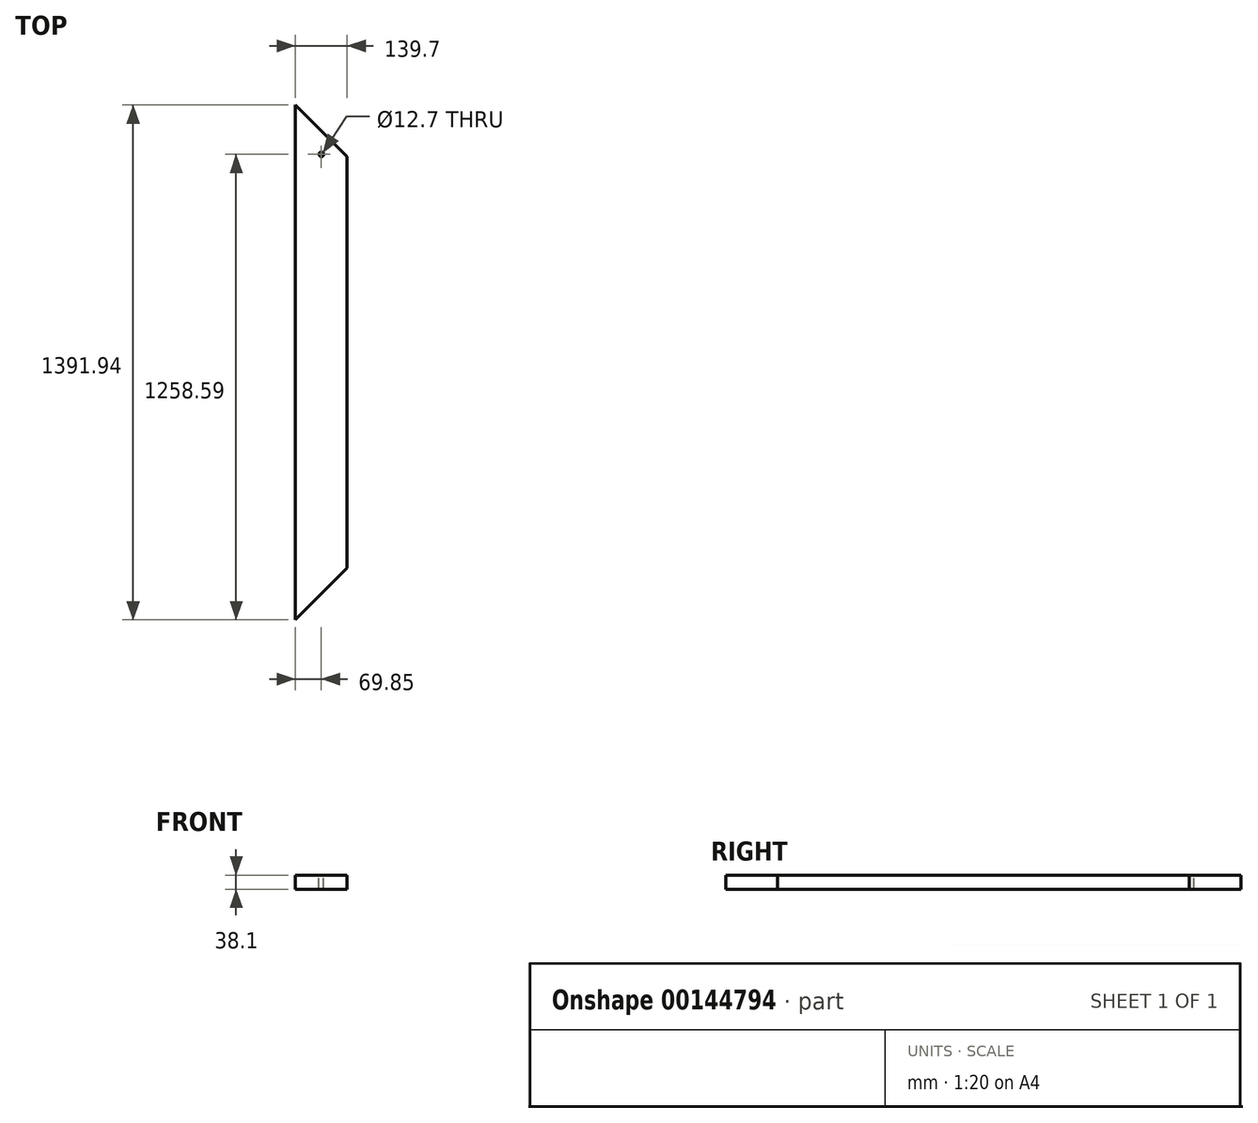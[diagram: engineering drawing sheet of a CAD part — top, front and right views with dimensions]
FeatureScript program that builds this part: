
annotation { "Feature Type Name" : "Feature", "Feature Type Description" : "" }
export const myFeature = defineFeature(function(context is Context, id is Id, definition is map)
    precondition{}
    {
        {
            var Q0;
            Q0=qCreatedBy(makeId("Front.planeOp"),FACE);
            var sketch = newSketch(context, id + "F0", { "sketchPlane" : qUnion([Q0])});
            skLineSegment(sketch, "E0.bottom", {"start": v(0, 0) * mm, "end": v(139.7, 0) * mm});
            skLineSegment(sketch, "E0.top", {"start": v(0, 38.1) * mm, "end": v(139.7, 38.1) * mm});
            skLineSegment(sketch, "E0.left", {"start": v(0, 0) * mm, "end": v(0, 38.1) * mm});
            skLineSegment(sketch, "E0.right", {"start": v(139.7, 0) * mm, "end": v(139.7, 38.1) * mm});
            skSolve(sketch);
        }
        {
            var Q0;
            Q0=makeQuery(id+"F0.imprint","IMPRINT",FACE,{"disambiguationData":[TD([[makeQuery(id+"F0.imprint","IMPRINT",EDGE,{"derivedFrom":sQuery(id+"F0.wireOp",EDGE,"E0.bottom")}),1.0]])]});
            extrude(context, id + "F1", {"entities" : qUnion([Q0]), "depth" : 1828.8 * mm});
        }
        {
            var Q0;
            Q0=makeQuery(id+"F1.opExtrude","CAP_FACE",FACE,{"disambiguationData":[OSD([sQuery(id+"F0.wireOp",EDGE,"E0.bottom"),sQuery(id+"F0.wireOp",EDGE,"E0.top"),sQuery(id+"F0.wireOp",EDGE,"E0.left"),sQuery(id+"F0.wireOp",EDGE,"E0.right")])],"isStart":false});
            var Q1;
            Q1=makeQuery(id+"F1.opExtrude","CAP_EDGE",EDGE,{"disambiguationData":[OSD([sQuery(id+"F0.wireOp",EDGE,"E0.right")])],"isStart":false});
            cPlane(context, id + "F2", {"entities" : qUnion([Q0, Q1]), "cplaneType" : CPlaneType.LINE_ANGLE, "offset" : 25.4 * mm, "angle" : 45 * degree, "width" : 152.4 * mm, "height" : 152.4 * mm});
        }
        {
            var Q0;
            Q0=qCreatedBy(id+"F2.planeOp",FACE);
            var sketch = newSketch(context, id + "F3", { "sketchPlane" : qUnion([Q0])});
            skLineSegment(sketch, "E1.bottom", {"start": v(1388.33, 137.34) * mm, "end": v(1057.01, 137.34) * mm});
            skLineSegment(sketch, "E1.top", {"start": v(1388.33, -123.24) * mm, "end": v(1057.01, -123.24) * mm});
            skLineSegment(sketch, "E1.left", {"start": v(1388.33, 137.34) * mm, "end": v(1388.33, -123.24) * mm});
            skLineSegment(sketch, "E1.right", {"start": v(1057.01, 137.34) * mm, "end": v(1057.01, -123.24) * mm});
            skSolve(sketch);
        }
        {
            var Q0;
            Q0=qSketchRegion(id+"F3",true);
            extrude(context, id + "F4", {"entities" : qUnion([Q0]), "operationType" : NewBodyOperationType.REMOVE, "depth" : 101.6 * mm});
        }
        {
            var Q0;
            Q0=makeQuery(id+"F4.boolean.opBoolean","INTERSECT",EDGE,{"derivedFrom":[makeQuery(id+"F1.opExtrude","SWEPT_FACE",FACE,{"disambiguationData":[OSD([sQuery(id+"F0.wireOp",EDGE,"E0.left")])]}),makeQuery(id+"F4.opExtrude","CAP_FACE",FACE,{"disambiguationData":[OSD([sQuery(id+"F3.wireOp",EDGE,"E1.bottom"),sQuery(id+"F3.wireOp",EDGE,"E1.top"),sQuery(id+"F3.wireOp",EDGE,"E1.left"),sQuery(id+"F3.wireOp",EDGE,"E1.right")])],"isStart":false})]});
            cPlane(context, id + "F5", {"entities" : qUnion([Q0]), "cplaneType" : CPlaneType.LINE_ANGLE, "offset" : 25.4 * mm, "angle" : 315 * degree, "width" : 152.4 * mm, "height" : 152.4 * mm});
        }
        {
            var Q0;
            Q0=qCreatedBy(id+"F5.planeOp",FACE);
            cPlane(context, id + "F6", {"entities" : qUnion([Q0]), "cplaneType" : CPlaneType.OFFSET, "offset" : 984.25 * mm, "oppositeDirection" : true, "width" : 152.4 * mm, "height" : 152.4 * mm});
        }
        {
            var Q0;
            Q0=qCreatedBy(id+"F6.planeOp",FACE);
            var sketch = newSketch(context, id + "F7", { "sketchPlane" : qUnion([Q0])});
            skLineSegment(sketch, "E2.bottom", {"start": v(-162.29, 396.16) * mm, "end": v(1391.17, 396.16) * mm});
            skLineSegment(sketch, "E2.top", {"start": v(-162.29, -759.2) * mm, "end": v(1391.17, -759.2) * mm});
            skLineSegment(sketch, "E2.left", {"start": v(-162.29, 396.16) * mm, "end": v(-162.29, -759.2) * mm});
            skLineSegment(sketch, "E2.right", {"start": v(1391.17, 396.16) * mm, "end": v(1391.17, -759.2) * mm});
            skSolve(sketch);
        }
        {
            var Q0;
            Q0=makeQuery(id+"F7.imprint","IMPRINT",FACE,{"disambiguationData":[TD([[makeQuery(id+"F7.imprint","IMPRINT",EDGE,{"derivedFrom":sQuery(id+"F7.wireOp",EDGE,"E2.bottom")}),-1.0]])]});
            extrude(context, id + "F8", {"entities" : qUnion([Q0]), "operationType" : NewBodyOperationType.REMOVE, "oppositeDirection" : true, "depth" : 762 * mm});
        }
        {
            var Q0;
            Q0=makeQuery(id+"F1.opExtrude","SWEPT_FACE",FACE,{"disambiguationData":[OSD([sQuery(id+"F0.wireOp",EDGE,"E0.top")])]});
            var sketch = newSketch(context, id + "F9", { "sketchPlane" : qUnion([Q0])});
            skCircle(sketch, "E3", {"center": v(69.85, -566.23) * mm, "radius": 6.35 * mm});
            skSolve(sketch);
        }
        {
            var Q0;
            Q0=makeQuery(id+"F9.imprint","IMPRINT",FACE,{"disambiguationData":[TD([[makeQuery(id+"F9.imprint","IMPRINT",EDGE,{"derivedFrom":sQuery(id+"F9.wireOp",EDGE,"E3")}),1.0]])]});
            extrude(context, id + "F10", {"entities" : qUnion([Q0]), "operationType" : NewBodyOperationType.REMOVE, "endBound" : BoundingType.THROUGH_ALL, "oppositeDirection" : true, "depth" : 25.4 * mm});
        }
    });
